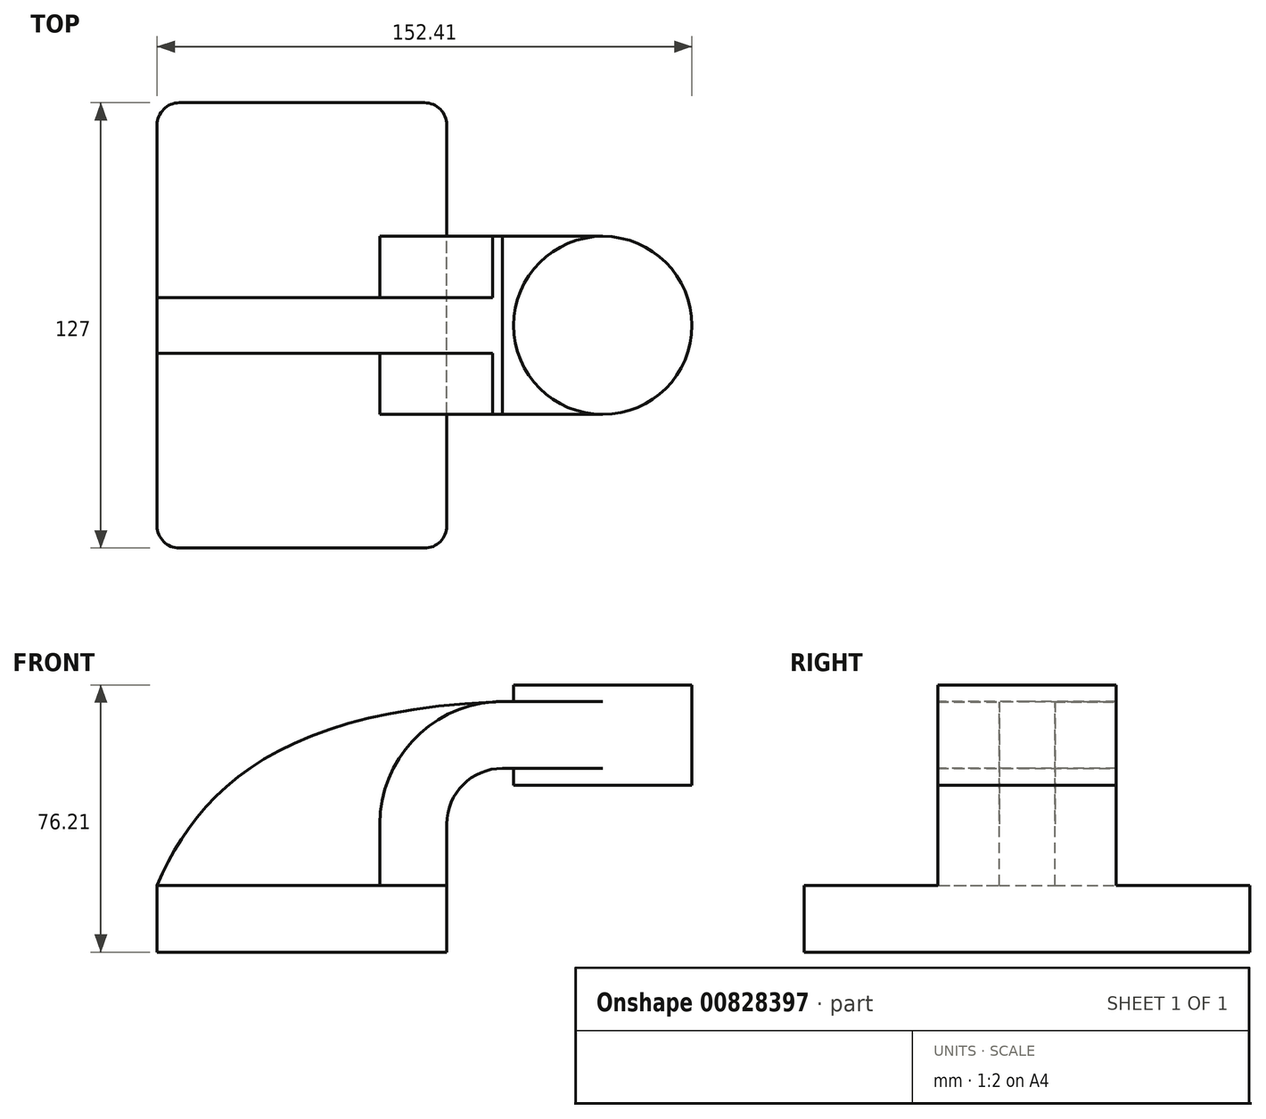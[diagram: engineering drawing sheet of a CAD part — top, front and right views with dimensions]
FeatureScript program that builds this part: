
annotation { "Feature Type Name" : "Feature", "Feature Type Description" : "" }
export const myFeature = defineFeature(function(context is Context, id is Id, definition is map)
    precondition{}
    {
        {
            var Q0;
            Q0=qCreatedBy(makeId("Front.planeOp"),FACE);
            var sketch = newSketch(context, id + "F0", { "sketchPlane" : qUnion([Q0])});
            skLineSegment(sketch, "E0.bottom", {"start": v(-41.28, -9.52) * mm, "end": v(41.28, -9.52) * mm});
            skLineSegment(sketch, "E0.top", {"start": v(-41.28, 9.52) * mm, "end": v(41.28, 9.52) * mm});
            skLineSegment(sketch, "E0.left", {"start": v(-41.28, -9.52) * mm, "end": v(-41.28, 9.52) * mm});
            skLineSegment(sketch, "E0.right", {"start": v(41.28, -9.53) * mm, "end": v(41.28, 9.52) * mm});
            skPoint(sketch, "E0.middle", {"position": v(0, 0) * mm});
            skLineSegment(sketch, "E1.bottom", {"start": v(60.33, 38.1) * mm, "end": v(111.13, 38.1) * mm});
            skLineSegment(sketch, "E1.top", {"start": v(60.33, 66.68) * mm, "end": v(111.13, 66.68) * mm});
            skLineSegment(sketch, "E1.left", {"start": v(60.33, 38.1) * mm, "end": v(60.33, 66.68) * mm});
            skLineSegment(sketch, "E1.right", {"start": v(111.13, 38.1) * mm, "end": v(111.13, 66.68) * mm});
            skPoint(sketch, "E1.middle", {"position": v(85.73, 52.39) * mm});
            skLineSegment(sketch, "E2", {"start": v(41.28, 9.52) * mm, "end": v(41.28, 27) * mm});
            skArc(sketch, "E3", {"start": v(41.28, 27) * mm, "mid": v(45.92, 38.23) * mm, "end": v(57.15, 42.88) * mm});
            skLineSegment(sketch, "E4", {"start": v(57.15, 42.88) * mm, "end": v(85.73, 42.88) * mm});
            skPoint(sketch, "E4.endSnap0", {"position": v(85.73, 38.1) * mm});
            skLineSegment(sketch, "E5.0", {"start": v(57.15, 61.93) * mm, "end": v(85.73, 61.93) * mm});
            skArc(sketch, "E5.1", {"start": v(22.23, 27) * mm, "mid": v(32.45, 51.7) * mm, "end": v(57.15, 61.93) * mm});
            skLineSegment(sketch, "E5.2", {"start": v(22.23, 9.52) * mm, "end": v(22.23, 27) * mm});
            skLineSegment(sketch, "E6", {"start": v(85.73, 38.1) * mm, "end": v(85.73, 66.68) * mm});
            skFitSpline(sketch, "E7", {"points": [v(-41.28, 9.53) * mm, v(57.15, 61.93) * mm], "startDerivative": vector(33.81, 78.45) * mm, "endDerivative": vector(194.04, 6.82) * mm});
            skSolve(sketch);
        }
        {
            var Q0;
            Q0=makeQuery(id+"F0.imprint","IMPRINT",FACE,{"disambiguationData":[TD([[makeQuery(id+"F0.imprint","IMPRINT",EDGE,{"derivedFrom":sQuery(id+"F0.wireOp",EDGE,"E0.bottom")}),1.0]])]});
            extrude(context, id + "F1", {"entities" : qUnion([Q0]), "endBound" : BoundingType.SYMMETRIC, "depth" : 127 * mm, "offsetDistance" : 25.4 * mm});
        }
        {
            var Q0;
            {var subQ1=sQuery(id+"F0.wireOp",EDGE,"E2");Q0=makeQuery(id+"F0.imprint","IMPRINT",FACE,{"disambiguationData":[TD([[makeQuery(id+"F0.imprint","IMPRINT",EDGE,{"derivedFrom":subQ1}),1.0]])]});}
            var Q1;
            {var subQ0=sQuery(id+"F0.wireOp",EDGE,"E4");var subQ1=sQuery(id+"F0.wireOp",EDGE,"E1.left");var subQ2=makeQuery(id+"F0.imprint","INTERSECT",VERTEX,{"derivedFrom":[subQ1,subQ0]});Q1=makeQuery(id+"F0.imprint","IMPRINT",FACE,{"disambiguationData":[TD([[makeQuery(id+"F0.imprint","IMPRINT",EDGE,{"disambiguationData":[TD([[subQ2,-1.0]])],"derivedFrom":subQ1}),-1.0]])]});}
            extrude(context, id + "F2", {"entities" : qUnion([Q0, Q1]), "operationType" : NewBodyOperationType.ADD, "endBound" : BoundingType.SYMMETRIC, "depth" : 50.8 * mm, "offsetDistance" : 25.4 * mm});
        }
        {
            var Q0;
            {var subQ3=sQuery(id+"F0.wireOp",EDGE,"E5.2");Q0=makeQuery(id+"F0.imprint","IMPRINT",FACE,{"disambiguationData":[TD([[makeQuery(id+"F0.imprint","IMPRINT",EDGE,{"derivedFrom":subQ3}),1.0]])]});}
            extrude(context, id + "F3", {"entities" : qUnion([Q0]), "operationType" : NewBodyOperationType.ADD, "endBound" : BoundingType.SYMMETRIC, "depth" : 15.88 * mm, "offsetDistance" : 25.4 * mm});
        }
        {
            var Q0;
            {var subQ4=sQuery(id+"F0.wireOp",EDGE,"E1.right");Q0=makeQuery(id+"F0.imprint","IMPRINT",FACE,{"disambiguationData":[TD([[makeQuery(id+"F0.imprint","IMPRINT",EDGE,{"derivedFrom":subQ4}),1.0]])]});}
            var Q1;
            Q1=sQuery(id+"F0.wireOp",EDGE,"E6");
            revolve(context, id + "F4", {"operationType" : NewBodyOperationType.ADD, "surfaceOperationType" : NewSurfaceOperationType.NEW, "entities" : qUnion([Q0]), "axis" : qUnion([Q1]), "revolveType" : RevolveType.FULL});
        }
        {
            var Q0;
            Q0=makeQuery(id+"F1.opExtrude","CAP_EDGE",EDGE,{"disambiguationData":[OSD([sQuery(id+"F0.wireOp",EDGE,"E0.left")])],"isStart":false});
            var Q1;
            Q1=makeQuery(id+"F1.opExtrude","CAP_EDGE",EDGE,{"disambiguationData":[OSD([sQuery(id+"F0.wireOp",EDGE,"E0.right")])],"isStart":false});
            var Q2;
            Q2=makeQuery(id+"F1.opExtrude","CAP_EDGE",EDGE,{"disambiguationData":[OSD([sQuery(id+"F0.wireOp",EDGE,"E0.right")])],"isStart":true});
            var Q3;
            Q3=makeQuery(id+"F1.opExtrude","CAP_EDGE",EDGE,{"disambiguationData":[OSD([sQuery(id+"F0.wireOp",EDGE,"E0.left")])],"isStart":true});
            fillet(context, id + "F5", {"entities" : qUnion([Q0, Q1, Q2, Q3]), "radius" : 6.35 * mm, "tangentPropagation" : true, "allowEdgeOverflow" : false});
        }
    });
